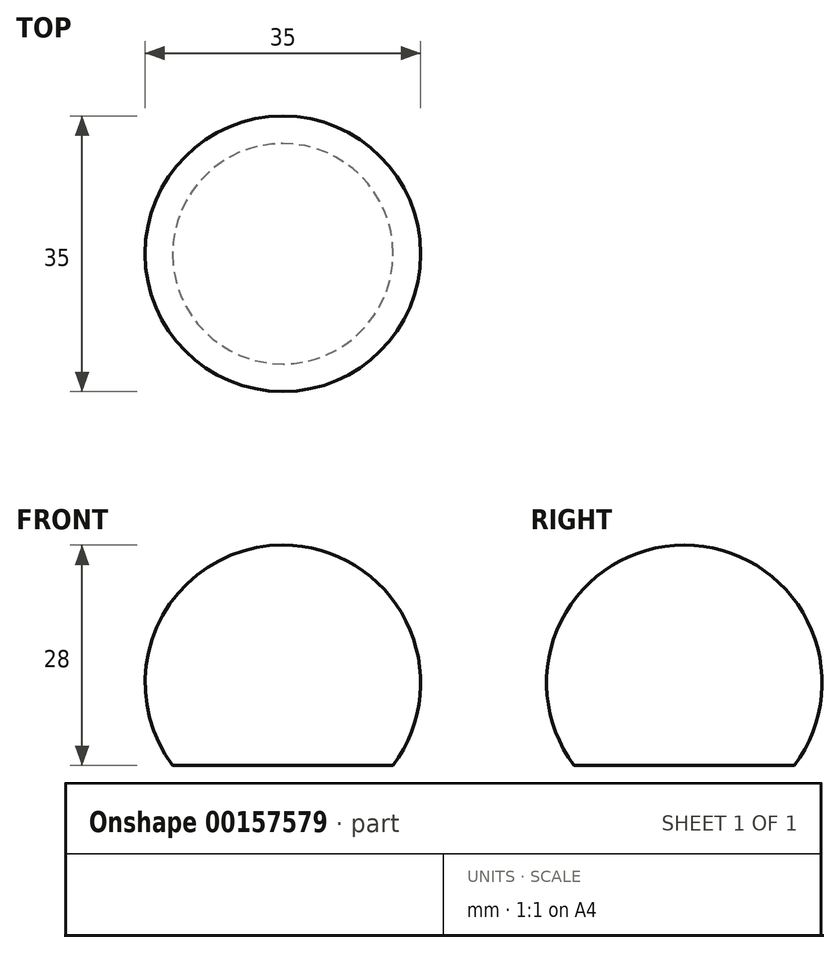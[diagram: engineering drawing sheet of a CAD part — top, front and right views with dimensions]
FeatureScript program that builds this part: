
annotation { "Feature Type Name" : "Feature", "Feature Type Description" : "" }
export const myFeature = defineFeature(function(context is Context, id is Id, definition is map)
    precondition{}
    {
        {
            var Q0;
            Q0=qCreatedBy(makeId("Front.planeOp"),FACE);
            var sketch = newSketch(context, id + "F0", { "sketchPlane" : qUnion([Q0])});
            skCircle(sketch, "E0", {"center": v(0, -17.5) * mm, "radius": 17.5 * mm});
            skLineSegment(sketch, "E1", {"start": v(0, -35) * mm, "end": v(0, 0) * mm});
            skSolve(sketch);
        }
        {
            var Q0;
            {var subQ0=sQuery(id+"F0.wireOp",EDGE,"E1");Q0=makeQuery(id+"F0.imprint","IMPRINT",FACE,{"disambiguationData":[TD([[makeQuery(id+"F0.imprint","IMPRINT",EDGE,{"derivedFrom":subQ0}),-1.0]])]});}
            var Q1;
            Q1=sQuery(id+"F0.wireOp",EDGE,"E1");
            revolve(context, id + "F1", {"entities" : qUnion([Q0]), "axis" : qUnion([Q1]), "revolveType" : RevolveType.FULL});
        }
        {
            var Q0;
            Q0=qCreatedBy(makeId("Top.planeOp"),FACE);
            var sketch = newSketch(context, id + "F2", { "sketchPlane" : qUnion([Q0])});
            skLineSegment(sketch, "E2.bottom", {"start": v(17.5, 17.5) * mm, "end": v(-17.5, 17.5) * mm});
            skLineSegment(sketch, "E2.top", {"start": v(17.5, -17.5) * mm, "end": v(-17.5, -17.5) * mm});
            skLineSegment(sketch, "E2.left", {"start": v(17.5, 17.5) * mm, "end": v(17.5, -17.5) * mm});
            skLineSegment(sketch, "E2.right", {"start": v(-17.5, 17.5) * mm, "end": v(-17.5, -17.5) * mm});
            skPoint(sketch, "E2.middle", {"position": v(0, 0) * mm});
            skSolve(sketch);
        }
        {
            var Q0;
            Q0 = qSketchRegion(id + "F2", true);
            extrude(context, id + "F3", {"entities" : qUnion([Q0]), "oppositeDirection" : true, "depth" : 28 * mm});
        }
        {
            var Q0;
            Q0=makeQuery(id+"F1.opRevolve","SWEPT_BODY",BODY,{"disambiguationData":[OSD([sQuery(id+"F0.wireOp",EDGE,"E0"),sQuery(id+"F0.wireOp",EDGE,"E1")])]});
            var Q1;
            Q1=makeQuery(id+"F3.opExtrude","SWEPT_BODY",BODY,{"disambiguationData":[OSD([sQuery(id+"F2.wireOp",EDGE,"E2.bottom"),sQuery(id+"F2.wireOp",EDGE,"E2.top"),sQuery(id+"F2.wireOp",EDGE,"E2.left"),sQuery(id+"F2.wireOp",EDGE,"E2.right")])]});
            booleanBodies(context, id + "F4", {"operationType" : BooleanOperationType.INTERSECTION, "tools" : qUnion([Q0, Q1])});
        }
    });
